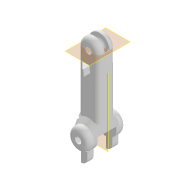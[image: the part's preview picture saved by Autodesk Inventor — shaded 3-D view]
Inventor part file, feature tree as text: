
AUTODESK INVENTOR PART (.ipt)
format: ipt  version: 2020.2 (Build 242310000, 310)  size: 331,776 bytes
history: native  units: mm
features: sketch x9, extrude x5, mirror x3, plane x2, chamfer x2, fillet x2, thread x1, sweep x1
ambient origin geometry x8: Origin, YZ Plane, XZ Plane, XY Plane, X Axis, Y Axis, Z Axis, Center Point
bodies: Solid1 (feature_tree)
feature tree (25):
  extrude  "base"  Depth=10.0mm
  extrude  "joint"  Depth=3.0mm
  plane  "Work Plane1"
  mirror  "Mirror1"
  chamfer  "Chamfer1"  Distance=8.0mm
  extrude  "joint_2"  Depth=10.0mm
  fillet  "Fillet1"  Radius=5.0mm
  plane  "Work Plane2"
  thread  "thread_hole_end"  [1 undecoded]
  extrude  "lock_1"  Depth=9.0mm TaperAngle=0.0deg
  mirror  "Mirror2"
  fillet  "Fillet3"  Radius=2.0mm
  extrude  "lock_2"  Depth=5.25mm
  mirror  "Mirror3"
  chamfer  "Chamfer2"  Distance=25.0mm
  sweep  "Sweep1"
  sketch  "Sketch1"  dims[d0=3.0mm d1=10.0mm]
  sketch  "Sketch2"  dims[d2=35.0mm d3=3.0mm]
  sketch  "Sketch3"  dims[d4=10.0mm d5=8.0mm d6=0.0mm]
  sketch  "Sketch5"  dims[d7=3.0mm d8=10.0mm d9=5.0mm d10=0.0mm d11=2.0mm d12=2.0mm d13=45.0deg]
  sketch  "Sketch6"  dims[d14=10.5mm d15=9.0mm d16=0.0mm d17=2.0mm]
  sketch  "Sketch8"  dims[d21=10.0mm d22=5.25mm]
  sketch  "Sketch9"  dims[d23=3.5mm]
  sketch  "Sketch10"  dims[d24=3.5mm]
  sketch  "Sketch11"  dims[d26=2.5mm d27=25.0mm d28=0.0mm d29=3.5mm d30=2.5mm d31=180.0deg d35=5.0mm d36=3.0mm d37=3.0mm d38=0.0mm d40=3.0mm d41=6.0mm d42=3.0mm d43=14.835299mm d44=3.0mm d45=0.0mm d46=3.0mm d47=2.0mm d48=45.0deg d49=3.5mm d50=10.0mm d52=3.5mm d54=3.0mm d55=0.0mm d56=0.0mm]
note: 1 required parameter value undecoded (feature->parameter linkage not recoverable at this tier; creation-order binding heuristic only, values carry confidence <= 0.55)
